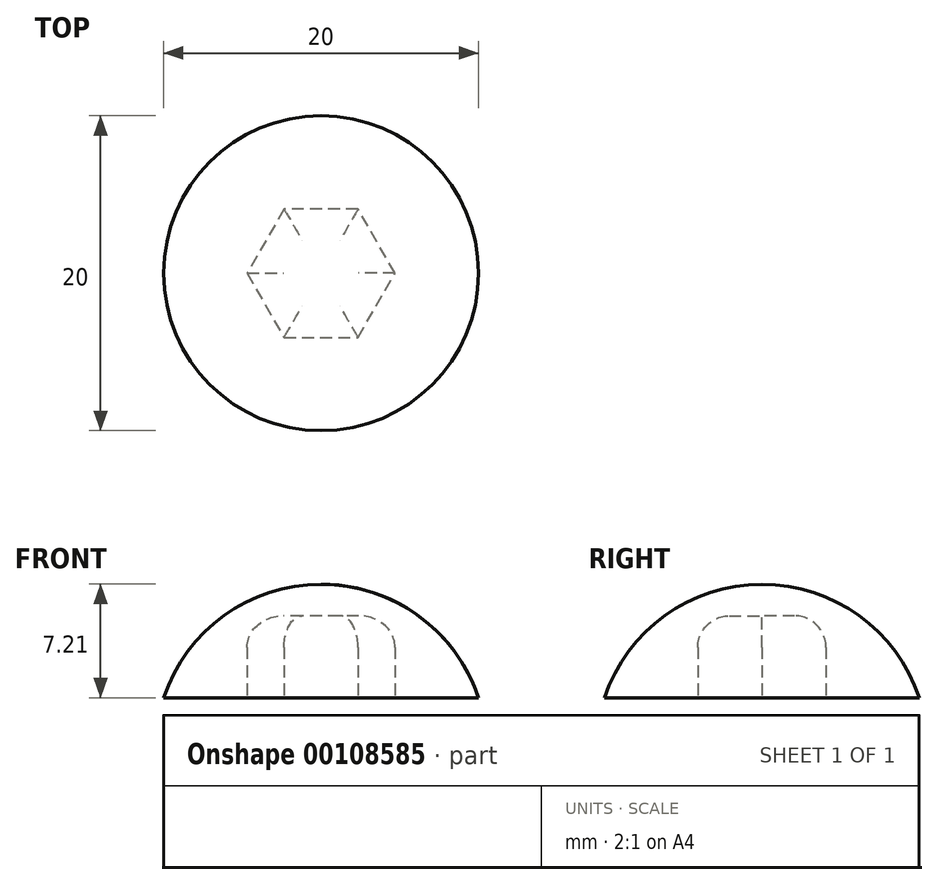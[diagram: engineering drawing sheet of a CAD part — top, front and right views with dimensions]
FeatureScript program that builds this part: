
annotation { "Feature Type Name" : "Feature", "Feature Type Description" : "" }
export const myFeature = defineFeature(function(context is Context, id is Id, definition is map)
    precondition{}
    {
        {
            assignVariable(context, id + "F0", {"name" : "H", "anyValue" : 4.2});
        }
        {
            var Q0;
            Q0=qCreatedBy(makeId("Front.planeOp"),FACE);
            var sketch = newSketch(context, id + "F1", { "sketchPlane" : qUnion([Q0])});
            skArc(sketch, "E0", {"start": v(10, 0) * mm, "mid": v(6.16, 5.22) * mm, "end": v(0, 7.2) * mm, "construction": true});
            skLineSegment(sketch, "E1", {"start": v(-10, 0) * mm, "end": v(0, 0) * mm});
            skLineSegment(sketch, "E2", {"start": v(0, 0) * mm, "end": v(0, 7.2) * mm});
            skLineSegment(sketch, "E3", {"start": v(-4.5, 0) * mm, "end": v(-4.5, 6.2) * mm, "construction": true});
            skArc(sketch, "E4", {"start": v(0, 7.2) * mm, "mid": v(-6.16, 5.22) * mm, "end": v(-10, 0) * mm});
            skLineSegment(sketch, "E5", {"start": v(0, 0) * mm, "end": v(10, 0) * mm, "construction": true});
            skSolve(sketch);
        }
        {
            var Q0;
            Q0 = qSketchRegion(id + "F1", true);
            var Q1;
            Q1=sQuery(id+"F1.wireOp",EDGE,"E2");
            revolve(context, id + "F2", {"entities" : qUnion([Q0]), "axis" : qUnion([Q1]), "revolveType" : RevolveType.FULL});
        }
        {
            var Q0;
            Q0=makeQuery(id+"F2.opRevolve","SWEPT_FACE",FACE,{"disambiguationData":[OSD([sQuery(id+"F1.wireOp",EDGE,"E1")])]});
            var sketch = newSketch(context, id + "F3", { "sketchPlane" : qUnion([Q0])});
            skCircle(sketch, "E6.cCircle", {"center": v(0, 0) * mm, "radius": 4.7 * mm, "construction": true});
            skLineSegment(sketch, "E6.0", {"start": v(-2.35, 4.07) * mm, "end": v(2.35, 4.07) * mm});
            skLineSegment(sketch, "E6.1", {"start": v(2.35, 4.07) * mm, "end": v(4.7, 0) * mm});
            skLineSegment(sketch, "E6.2", {"start": v(4.7, 0) * mm, "end": v(2.35, -4.07) * mm});
            skLineSegment(sketch, "E6.3", {"start": v(2.35, -4.07) * mm, "end": v(-2.35, -4.07) * mm});
            skLineSegment(sketch, "E6.4", {"start": v(-2.35, -4.07) * mm, "end": v(-4.7, 0) * mm});
            skLineSegment(sketch, "E6.5", {"start": v(-4.7, 0) * mm, "end": v(-2.35, 4.07) * mm});
            skSolve(sketch);
        }
        {
            var Q0;
            Q0=makeQuery(id+"F3.imprint","IMPRINT",FACE,{"disambiguationData":[TD([[makeQuery(id+"F3.imprint","IMPRINT",EDGE,{"derivedFrom":sQuery(id+"F3.wireOp",EDGE,"E6.0")}),-1.0]])]});
            extrude(context, id + "F4", {"entities" : qUnion([Q0]), "operationType" : NewBodyOperationType.REMOVE, "oppositeDirection" : true, "depth" : (getVariable(context, 'H') + 1) * mm});
        }
        {
            var Q0;
            Q0=makeQuery(id+"F4.boolean.opBoolean","COPY",EDGE,{"derivedFrom":makeQuery(id+"F4.opExtrude","CAP_EDGE",EDGE,{"disambiguationData":[OSD([sQuery(id+"F3.wireOp",EDGE,"E6.0")])],"isStart":false})});
            var Q1;
            Q1=makeQuery(id+"F4.boolean.opBoolean","COPY",EDGE,{"derivedFrom":makeQuery(id+"F4.opExtrude","CAP_EDGE",EDGE,{"disambiguationData":[OSD([sQuery(id+"F3.wireOp",EDGE,"E6.5")])],"isStart":false})});
            var Q2;
            Q2=makeQuery(id+"F4.boolean.opBoolean","COPY",EDGE,{"derivedFrom":makeQuery(id+"F4.opExtrude","CAP_EDGE",EDGE,{"disambiguationData":[OSD([sQuery(id+"F3.wireOp",EDGE,"E6.1")])],"isStart":false})});
            var Q3;
            Q3=makeQuery(id+"F4.boolean.opBoolean","COPY",EDGE,{"derivedFrom":makeQuery(id+"F4.opExtrude","CAP_EDGE",EDGE,{"disambiguationData":[OSD([sQuery(id+"F3.wireOp",EDGE,"E6.2")])],"isStart":false})});
            var Q4;
            Q4=makeQuery(id+"F4.boolean.opBoolean","COPY",EDGE,{"derivedFrom":makeQuery(id+"F4.opExtrude","CAP_EDGE",EDGE,{"disambiguationData":[OSD([sQuery(id+"F3.wireOp",EDGE,"E6.4")])],"isStart":false})});
            var Q5;
            Q5=makeQuery(id+"F4.boolean.opBoolean","COPY",EDGE,{"derivedFrom":makeQuery(id+"F4.opExtrude","CAP_EDGE",EDGE,{"disambiguationData":[OSD([sQuery(id+"F3.wireOp",EDGE,"E6.3")])],"isStart":false})});
            fillet(context, id + "F5", {"entities" : qUnion([Q0, Q1, Q2, Q3, Q4, Q5]), "radius" : 2 * mm, "tangentPropagation" : true, "allowEdgeOverflow" : false});
        }
    });
